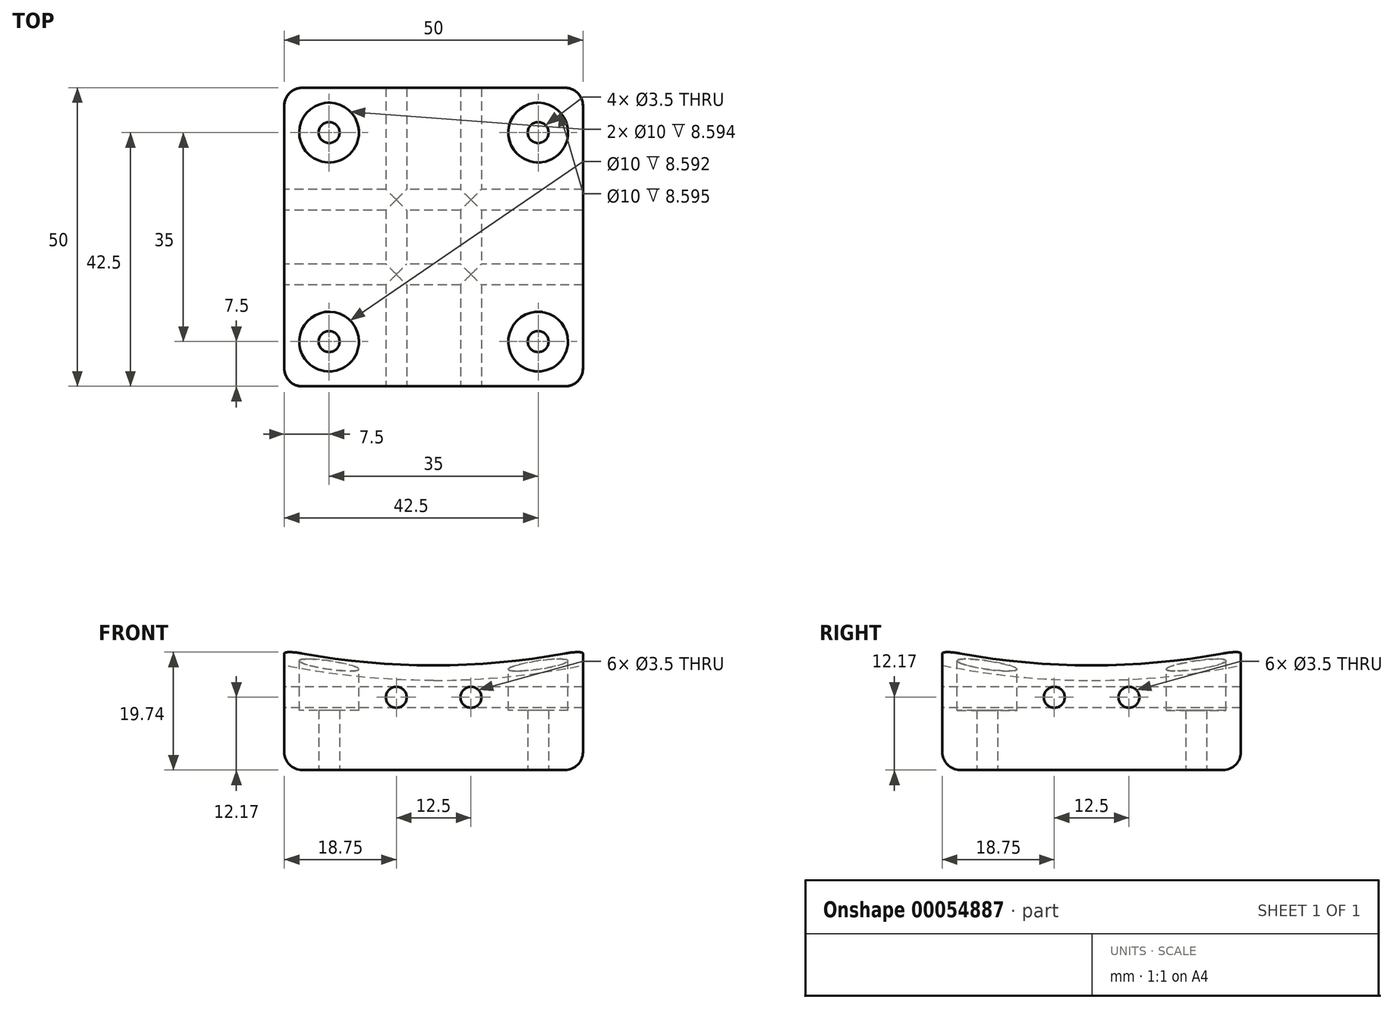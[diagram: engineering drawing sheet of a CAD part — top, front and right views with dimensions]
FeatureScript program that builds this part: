
annotation { "Feature Type Name" : "Feature", "Feature Type Description" : "" }
export const myFeature = defineFeature(function(context is Context, id is Id, definition is map)
    precondition{}
    {
        {
            var Q0;
            Q0=qCreatedBy(makeId("Top.planeOp"),FACE);
            var sketch = newSketch(context, id + "F0", { "sketchPlane" : qUnion([Q0])});
            skLineSegment(sketch, "E0.bottom", {"start": v(-25, 25) * mm, "end": v(25, 25) * mm});
            skLineSegment(sketch, "E0.top", {"start": v(-25, -25) * mm, "end": v(25, -25) * mm});
            skLineSegment(sketch, "E0.left", {"start": v(-25, 25) * mm, "end": v(-25, -25) * mm});
            skLineSegment(sketch, "E0.right", {"start": v(25, 25) * mm, "end": v(25, -25) * mm});
            skSolve(sketch);
        }
        {
            var Q0;
            Q0 = qSketchRegion(id + "F0", true);
            extrude(context, id + "F1", {"entities" : qUnion([Q0]), "depth" : 30 * mm});
        }
        {
            var Q0;
            Q0=qCreatedBy(makeId("Front.planeOp"),FACE);
            var sketch = newSketch(context, id + "F2", { "sketchPlane" : qUnion([Q0])});
            skArc(sketch, "E1", {"start": v(0, 15) * mm, "mid": v(125, 140) * mm, "end": v(0, 265) * mm});
            skLineSegment(sketch, "E2", {"start": v(0, 265) * mm, "end": v(0, 15) * mm, "construction": true});
            skLineSegment(sketch, "E3", {"start": v(0, 15) * mm, "end": v(0, 265) * mm});
            skSolve(sketch);
        }
        {
            var Q0;
            Q0 = qSketchRegion(id + "F2", true);
            var Q1;
            Q1=sQuery(id+"F2.wireOp",EDGE,"E3");
            revolve(context, id + "F3", {"operationType" : NewBodyOperationType.REMOVE, "entities" : qUnion([Q0]), "axis" : qUnion([Q1]), "revolveType" : RevolveType.FULL, "oppositeDirection" : true});
        }
        {
            var Q0;
            Q0=makeQuery(id+"F1.opExtrude","SWEPT_FACE",FACE,{"disambiguationData":[OSD([sQuery(id+"F0.wireOp",EDGE,"E0.left")])]});
            var sketch = newSketch(context, id + "F4", { "sketchPlane" : qUnion([Q0])});
            skCircle(sketch, "E4", {"center": v(-6.25, 12.17) * mm, "radius": 1.75 * mm});
            skCircle(sketch, "E5.MirrorC", {"center": v(6.25, 12.17) * mm, "radius": 1.75 * mm});
            skSolve(sketch);
        }
        {
            var Q0;
            Q0 = qSketchRegion(id + "F4", true);
            extrude(context, id + "F5", {"entities" : qUnion([Q0]), "operationType" : NewBodyOperationType.REMOVE, "endBound" : BoundingType.THROUGH_ALL, "oppositeDirection" : true, "depth" : 25 * mm});
        }
        {
            var Q0;
            Q0=makeQuery(id+"F1.opExtrude","SWEPT_FACE",FACE,{"disambiguationData":[OSD([sQuery(id+"F0.wireOp",EDGE,"E0.top")])]});
            var sketch = newSketch(context, id + "F6", { "sketchPlane" : qUnion([Q0])});
            skCircle(sketch, "E6", {"center": v(-6.25, 12.17) * mm, "radius": 1.75 * mm});
            skCircle(sketch, "E7.MirrorC", {"center": v(6.25, 12.17) * mm, "radius": 1.75 * mm});
            skSolve(sketch);
        }
        {
            var Q0;
            Q0 = qSketchRegion(id + "F6", true);
            extrude(context, id + "F7", {"entities" : qUnion([Q0]), "operationType" : NewBodyOperationType.REMOVE, "endBound" : BoundingType.THROUGH_ALL, "oppositeDirection" : true, "depth" : 25 * mm});
        }
        {
            var Q0;
            Q0=qCreatedBy(makeId("Top.planeOp"),FACE);
            var sketch = newSketch(context, id + "F8", { "sketchPlane" : qUnion([Q0])});
            skCircle(sketch, "E8", {"center": v(17.5, 17.5) * mm, "radius": 1.75 * mm});
            skCircle(sketch, "E9.0.1.0", {"center": v(17.5, -17.5) * mm, "radius": 1.75 * mm});
            skCircle(sketch, "E9.1.0.0", {"center": v(-17.5, 17.5) * mm, "radius": 1.75 * mm});
            skCircle(sketch, "E9.1.1.0", {"center": v(-17.5, -17.5) * mm, "radius": 1.75 * mm});
            skLineSegment(sketch, "E9.direction1", {"start": v(17.5, 17.5) * mm, "end": v(-17.5, 17.5) * mm, "construction": true});
            skLineSegment(sketch, "E9.direction2", {"start": v(17.5, 17.5) * mm, "end": v(17.5, -17.5) * mm, "construction": true});
            skSolve(sketch);
        }
        {
            var Q0;
            Q0 = qSketchRegion(id + "F8", true);
            extrude(context, id + "F9", {"entities" : qUnion([Q0]), "operationType" : NewBodyOperationType.REMOVE, "endBound" : BoundingType.THROUGH_ALL, "depth" : 25 * mm});
        }
        {
            var Q0;
            Q0=qCreatedBy(makeId("Top.planeOp"),FACE);
            cPlane(context, id + "F10", {"entities" : qUnion([Q0]), "cplaneType" : CPlaneType.OFFSET, "offset" : 30 * mm, "width" : 150 * mm, "height" : 150 * mm});
        }
        {
            var Q0;
            Q0=qCreatedBy(id+"F10.planeOp",FACE);
            var sketch = newSketch(context, id + "F11", { "sketchPlane" : qUnion([Q0])});
            skCircle(sketch, "E10", {"center": v(-17.5, 17.5) * mm, "radius": 5 * mm});
            skCircle(sketch, "E11.0.1.0", {"center": v(-17.5, -17.5) * mm, "radius": 5 * mm});
            skCircle(sketch, "E11.1.0.0", {"center": v(17.5, 17.5) * mm, "radius": 5 * mm});
            skCircle(sketch, "E11.1.1.0", {"center": v(17.5, -17.5) * mm, "radius": 5 * mm});
            skLineSegment(sketch, "E11.direction1", {"start": v(-17.5, 17.5) * mm, "end": v(17.5, 17.5) * mm, "construction": true});
            skLineSegment(sketch, "E11.direction2", {"start": v(-17.5, 17.5) * mm, "end": v(-17.5, -17.5) * mm, "construction": true});
            skSolve(sketch);
        }
        {
            var Q0;
            Q0 = qSketchRegion(id + "F11", true);
            extrude(context, id + "F12", {"entities" : qUnion([Q0]), "operationType" : NewBodyOperationType.REMOVE, "oppositeDirection" : true, "depth" : 20 * mm});
        }
        {
            var Q0;
            Q0=makeQuery(id+"F1.opExtrude","CAP_EDGE",EDGE,{"disambiguationData":[OSD([sQuery(id+"F0.wireOp",EDGE,"E0.left")])],"isStart":true});
            var Q1;
            Q1=makeQuery(id+"F1.opExtrude","CAP_EDGE",EDGE,{"disambiguationData":[OSD([sQuery(id+"F0.wireOp",EDGE,"E0.top")])],"isStart":true});
            var Q2;
            Q2=makeQuery(id+"F1.opExtrude","CAP_EDGE",EDGE,{"disambiguationData":[OSD([sQuery(id+"F0.wireOp",EDGE,"E0.right")])],"isStart":true});
            var Q3;
            Q3=makeQuery(id+"F1.opExtrude","CAP_EDGE",EDGE,{"disambiguationData":[OSD([sQuery(id+"F0.wireOp",EDGE,"E0.bottom")])],"isStart":true});
            var Q4;
            Q4=makeQuery(id+"F1.opExtrude","SWEPT_EDGE",EDGE,{"disambiguationData":[OSD([sQuery(id+"F0.wireOp",EDGE,"E0.top"),sQuery(id+"F0.wireOp",EDGE,"E0.right")])]});
            var Q5;
            Q5=makeQuery(id+"F1.opExtrude","SWEPT_EDGE",EDGE,{"disambiguationData":[OSD([sQuery(id+"F0.wireOp",EDGE,"E0.bottom"),sQuery(id+"F0.wireOp",EDGE,"E0.right")])]});
            var Q6;
            Q6=makeQuery(id+"F1.opExtrude","SWEPT_EDGE",EDGE,{"disambiguationData":[OSD([sQuery(id+"F0.wireOp",EDGE,"E0.bottom"),sQuery(id+"F0.wireOp",EDGE,"E0.left")])]});
            var Q7;
            Q7=makeQuery(id+"F1.opExtrude","SWEPT_EDGE",EDGE,{"disambiguationData":[OSD([sQuery(id+"F0.wireOp",EDGE,"E0.top"),sQuery(id+"F0.wireOp",EDGE,"E0.left")])]});
            fillet(context, id + "F13", {"entities" : qUnion([Q0, Q1, Q2, Q3, Q4, Q5, Q6, Q7]), "radius" : 3 * mm, "tangentPropagation" : true, "allowEdgeOverflow" : false});
        }
    });
